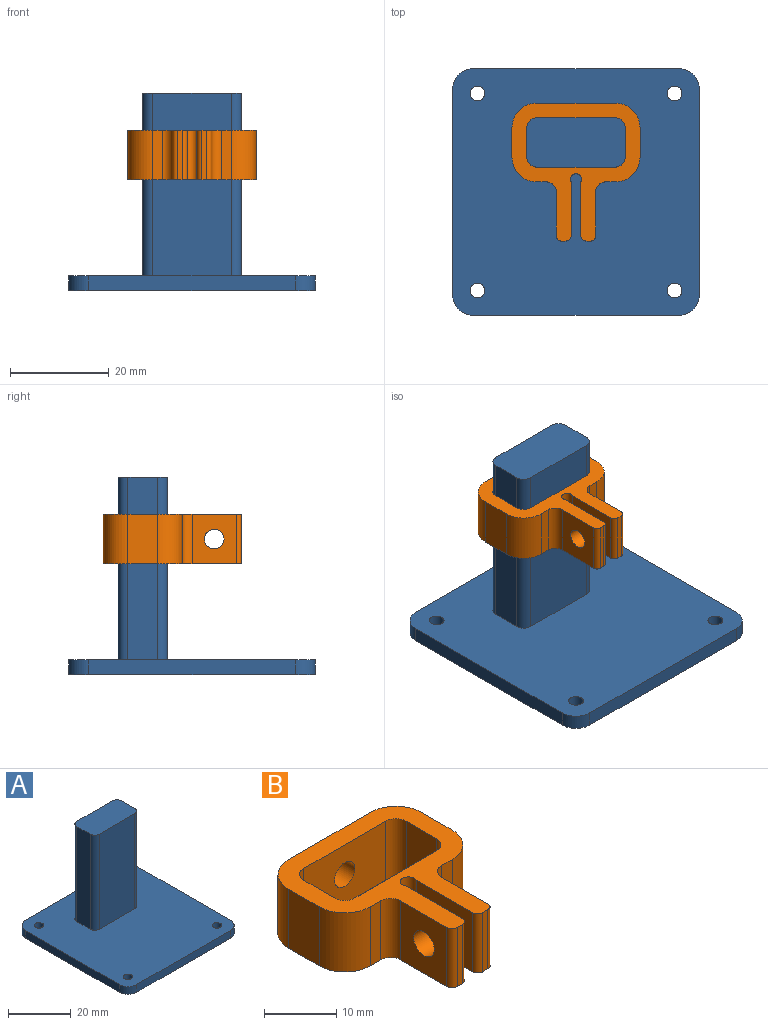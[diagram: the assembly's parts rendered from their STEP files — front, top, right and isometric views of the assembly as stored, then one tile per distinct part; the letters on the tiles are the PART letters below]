
ASSEMBLY  parts=2 mates=1
PART A: 23 faces, bbox 50x50x40 mm
  f0: plane 42x3mm, normal (0,-1,0), area 126mm2, adj f1,f7,f12,f13
  f1: cylinder r=4mm len=4mm, axis (0,0,-1), area 18.8mm2, adj f0,f2,f12,f13
  f2: plane 42x3mm, normal (1,0,0), area 126mm2, adj f1,f3,f12,f13
  f3: cylinder r=4mm len=4mm, axis (0,0,-1), area 18.8mm2, adj f2,f4,f12,f13
  f4: plane 42x3mm, normal (0,1,0), area 126mm2, adj f3,f5,f12,f13
  f5: cylinder r=4mm len=4mm, axis (0,0,-1), area 18.8mm2, adj f4,f6,f12,f13
  f6: plane 42x3mm, normal (-1,0,0), area 126mm2, adj f5,f7,f12,f13
  f7: cylinder r=4mm len=4mm, axis (0,0,-1), area 18.8mm2, adj f0,f6,f12,f13
  f8: cylinder r=1.5mm len=3mm, axis (0,0,-1), area 28.3mm2, adj f12,f13
  f9: cylinder r=1.5mm len=3mm, axis (0,0,-1), area 28.3mm2, adj f12,f13
  f10: cylinder r=1.5mm len=3mm, axis (0,0,-1), area 28.3mm2, adj f12,f13
  f11: cylinder r=1.5mm len=3mm, axis (0,0,-1), area 28.3mm2, adj f12,f13
  f12: plane 50x50mm, normal (0,0,1), area 2261.4mm2, adj f0,f1,f2,f3,f4,f5,f6,f7
  f13: plane 50x50mm, normal (0,0,-1), area 2458mm2, adj f0,f1,f2,f3,f4,f5,f6,f7
  f14: plane 20x10mm, normal (0,0,1), area 196.6mm2, adj f15,f16,f17,f18,f19,f20,f21,f22
  f15: cylinder r=2mm len=37mm, axis (0,0,-1), area 116.2mm2, adj f12,f14,f16,f22
  f16: plane 37x16mm, normal (0,-1,0), area 592mm2, adj f12,f14,f15,f17
  f17: cylinder r=2mm len=37mm, axis (0,0,-1), area 116.2mm2, adj f12,f14,f16,f18
  f18: plane 37x6mm, normal (-1,0,0), area 222mm2, adj f12,f14,f17,f19
  f19: cylinder r=2mm len=37mm, axis (0,0,-1), area 116.2mm2, adj f12,f14,f18,f20
  f20: plane 37x16mm, normal (0,1,0), area 592mm2, adj f12,f14,f19,f21
  f21: cylinder r=2mm len=37mm, axis (0,0,-1), area 116.2mm2, adj f12,f14,f20,f22
  f22: plane 37x6mm, normal (1,0,0), area 222mm2, adj f12,f14,f15,f21
PART B: 35 faces, bbox 26x28x10 mm
  f0: cylinder r=1mm len=10mm, axis (0,0,-1), area 15.7mm2, adj f1,f29,f30,f31
  f1: plane 10x1mm, normal (0,-1,0), area 10mm2, adj f0,f2,f30,f31
  f2: cylinder r=1mm len=10mm, axis (0,0,-1), area 15.7mm2, adj f1,f3,f30,f31
  f3: plane 10x9mm, normal (1,0,0), area 77.4mm2, adj f2,f4,f30,f31,f33
  f4: cylinder r=2mm len=10mm, axis (0,0,-1), area 31.4mm2, adj f3,f5,f30,f31
  f5: plane 10x2mm, normal (0,-1,0), area 20mm2, adj f4,f6,f30,f31
  f6: cylinder r=5mm len=10mm, axis (0,0,-1), area 78.5mm2, adj f5,f7,f30,f31
  f7: plane 10x6mm, normal (1,0,0), area 60mm2, adj f6,f8,f30,f31
  f8: cylinder r=5mm len=10mm, axis (0,0,-1), area 78.5mm2, adj f7,f9,f30,f31
  f9: plane 16x10mm, normal (0,1,0), area 147.4mm2, adj f8,f10,f30,f31,f32
  f10: cylinder r=5mm len=10mm, axis (0,0,-1), area 78.5mm2, adj f9,f11,f30,f31
  f11: plane 10x6mm, normal (-1,0,0), area 60mm2, adj f10,f12,f30,f31
  f12: cylinder r=5mm len=10mm, axis (0,0,-1), area 78.5mm2, adj f11,f13,f30,f31
  f13: plane 10x2mm, normal (0,-1,0), area 20mm2, adj f12,f14,f30,f31
  f14: cylinder r=2mm len=10mm, axis (0,0,-1), area 31.4mm2, adj f13,f15,f30,f31
  f15: plane 10x9mm, normal (-1,0,0), area 77.4mm2, adj f14,f16,f30,f31,f34
  f16: cylinder r=1mm len=10mm, axis (0,0,-1), area 15.7mm2, adj f15,f17,f30,f31
  f17: plane 10x1mm, normal (0,-1,0), area 10mm2, adj f16,f18,f30,f31
  f18: cylinder r=1mm len=10mm, axis (0,0,-1), area 15.7mm2, adj f17,f19,f30,f31
  f19: plane 11x10mm, normal (1,0,0), area 97.4mm2, adj f18,f20,f30,f31,f34
  f20: cylinder r=1.14mm len=10mm, axis (0,0,-1), area 46.9mm2, adj f19,f29,f30,f31
  f21: cylinder r=2mm len=10mm, axis (0,0,-1), area 31.4mm2, adj f22,f28,f30,f31
  f22: plane 10x6mm, normal (-1,0,0), area 60mm2, adj f21,f23,f30,f31
  f23: cylinder r=2mm len=10mm, axis (0,0,-1), area 31.4mm2, adj f22,f24,f30,f31
  f24: plane 16x10mm, normal (0,1,0), area 160mm2, adj f23,f25,f30,f31
  f25: cylinder r=2mm len=10mm, axis (0,0,-1), area 31.4mm2, adj f24,f26,f30,f31
  f26: plane 10x6mm, normal (1,0,0), area 60mm2, adj f25,f27,f30,f31
  f27: cylinder r=2mm len=10mm, axis (0,0,-1), area 31.4mm2, adj f26,f28,f30,f31
  f28: plane 16x10mm, normal (0,-1,0), area 147.4mm2, adj f21,f27,f30,f31,f32
  f29: plane 11x10mm, normal (-1,0,0), area 97.4mm2, adj f0,f20,f30,f31,f33
  f30: plane 28x26mm, normal (0,0,1), area 267.6mm2, adj f0,f1,f2,f3,f4,f5,f6,f7
  f31: plane 28x26mm, normal (0,0,-1), area 267.6mm2, adj f0,f1,f2,f3,f4,f5,f6,f7
  f32: cylinder r=2mm len=4mm, axis (0,1,0), area 37.7mm2, adj f9,f28
  f33: cylinder r=2mm len=4mm, axis (-1,0,0), area 37.7mm2, adj f3,f29
  f34: cylinder r=2mm len=4mm, axis (-1,0,0), area 37.7mm2, adj f15,f19
PLACE A at identity fixed
PLACE B t=(0,0,22.49)mm
MATE slider B.f30 <-> A.f14  axis (0,0,1) through (0,-5,32.49)mm
